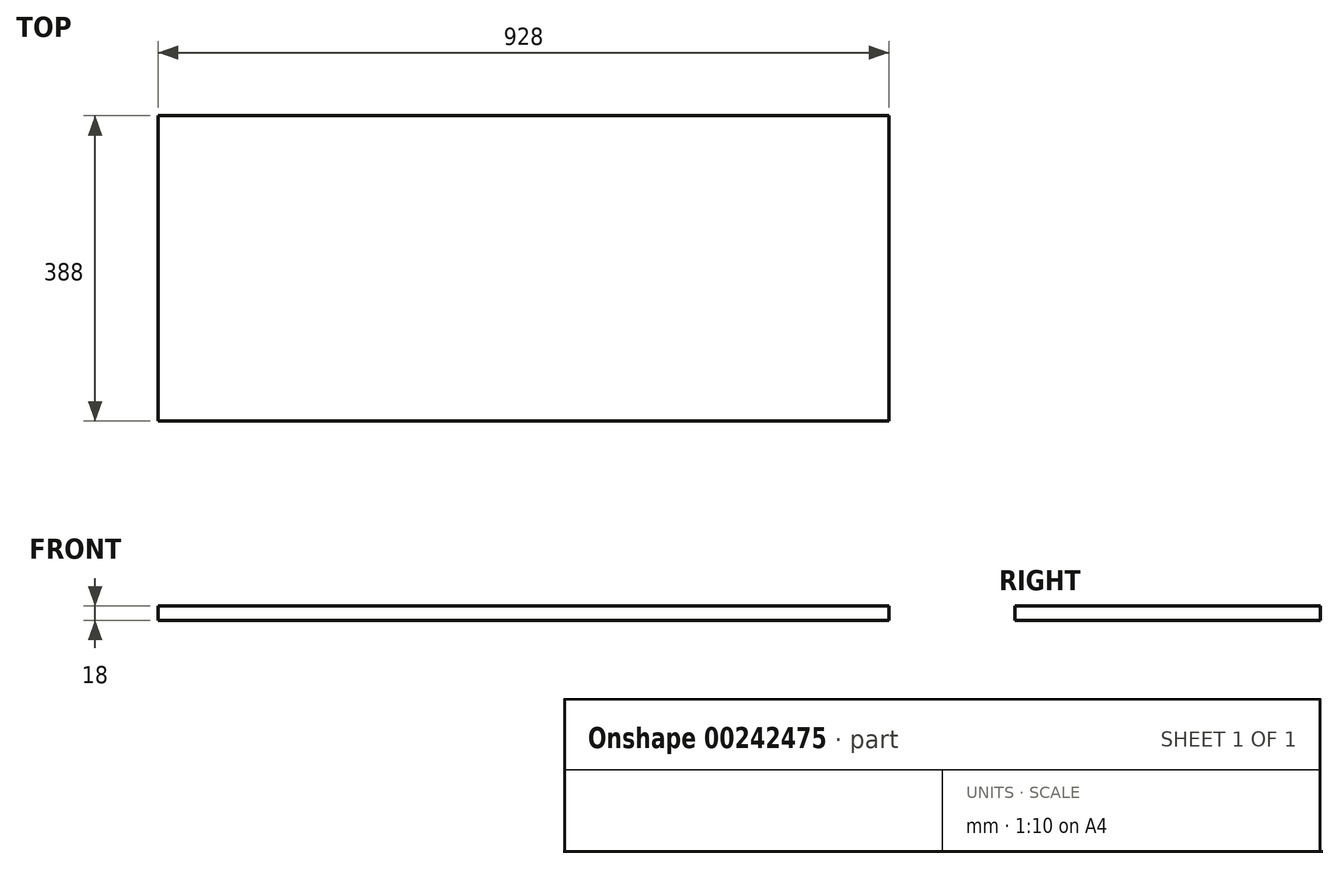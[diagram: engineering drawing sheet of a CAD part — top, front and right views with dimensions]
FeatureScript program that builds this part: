
annotation { "Feature Type Name" : "Feature", "Feature Type Description" : "" }
export const myFeature = defineFeature(function(context is Context, id is Id, definition is map)
    precondition{}
    {
        {
            var Q0;
            Q0=qCreatedBy(makeId("Top.planeOp"),FACE);
            var sketch = newSketch(context, id + "F0", { "sketchPlane" : qUnion([Q0])});
            skLineSegment(sketch, "E0.bottom", {"start": v(0, 0) * mm, "end": v(928, 0) * mm});
            skLineSegment(sketch, "E0.top", {"start": v(0, 388) * mm, "end": v(928, 388) * mm});
            skLineSegment(sketch, "E0.left", {"start": v(0, 0) * mm, "end": v(0, 388) * mm});
            skLineSegment(sketch, "E0.right", {"start": v(928, 0) * mm, "end": v(928, 388) * mm});
            skSolve(sketch);
        }
        {
            var Q0;
            Q0=makeQuery(id+"F0.imprint","IMPRINT",FACE,{"disambiguationData":[TD([[makeQuery(id+"F0.imprint","IMPRINT",EDGE,{"derivedFrom":sQuery(id+"F0.wireOp",EDGE,"E0.bottom")}),1.0]])]});
            extrude(context, id + "F1", {"entities" : qUnion([Q0]), "depth" : 18 * mm});
        }
    });
